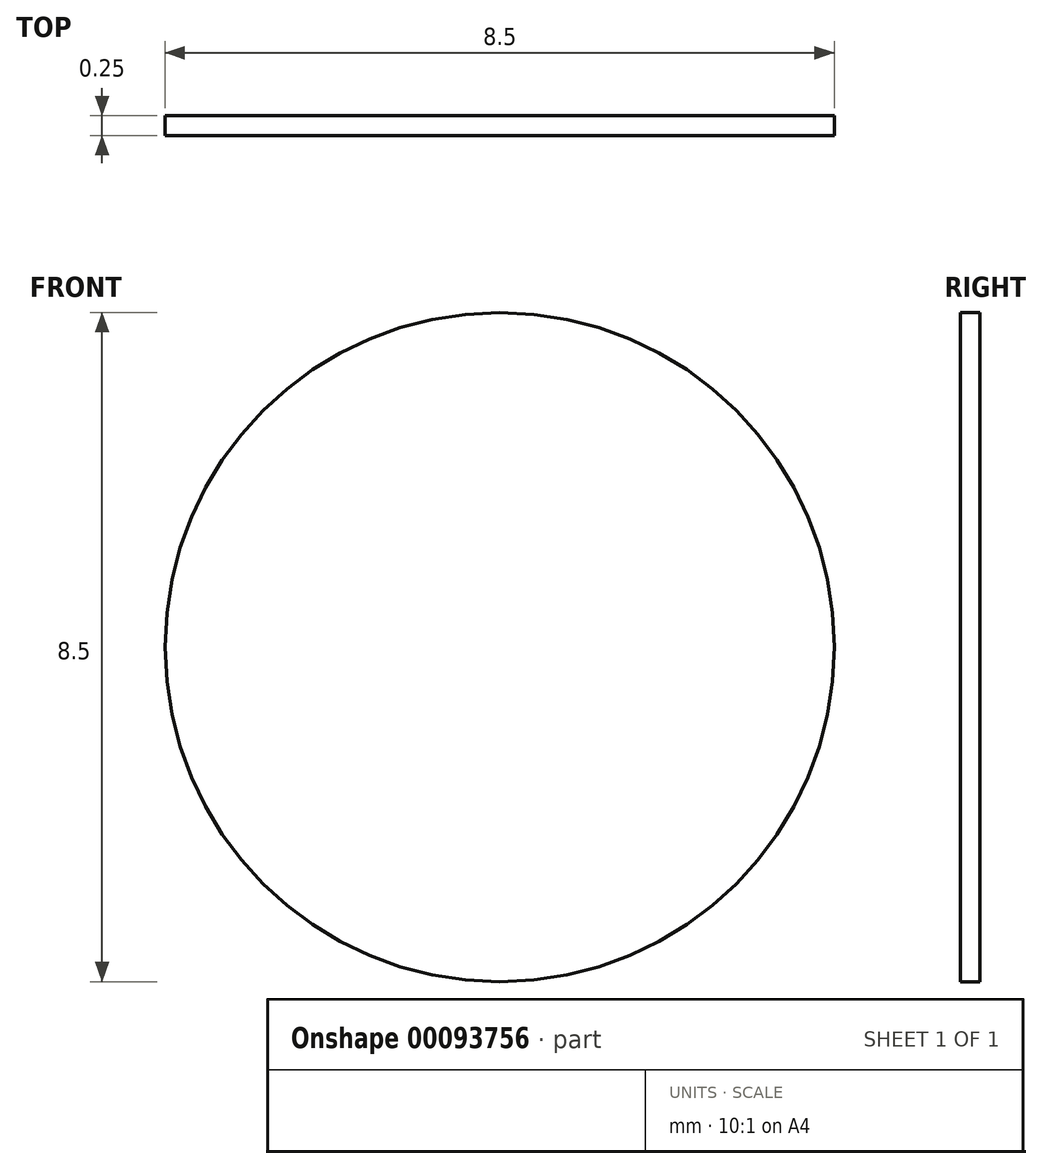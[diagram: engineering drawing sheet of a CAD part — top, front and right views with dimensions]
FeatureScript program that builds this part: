
annotation { "Feature Type Name" : "Feature", "Feature Type Description" : "" }
export const myFeature = defineFeature(function(context is Context, id is Id, definition is map)
    precondition{}
    {
        {
            var Q0;
            Q0=qCreatedBy(makeId("Front.planeOp"),FACE);
            var sketch = newSketch(context, id + "F0", { "sketchPlane" : qUnion([Q0])});
            skCircle(sketch, "E0", {"center": v(0, 0) * mm, "radius": 4.25 * mm});
            skSolve(sketch);
        }
        {
            var Q0;
            Q0=makeQuery(id+"F0.imprint","IMPRINT",FACE,{"disambiguationData":[TD([[makeQuery(id+"F0.imprint","IMPRINT",EDGE,{"derivedFrom":sQuery(id+"F0.wireOp",EDGE,"E0")}),1.0]])]});
            extrude(context, id + "F1", {"entities" : qUnion([Q0]), "oppositeDirection" : true, "depth" : 0.25 * mm});
        }
    });
